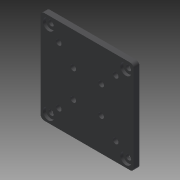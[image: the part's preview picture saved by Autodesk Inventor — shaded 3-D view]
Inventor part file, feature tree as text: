
AUTODESK INVENTOR PART (.ipt)
format: ipt  version: 2015 (Build 190159000, 159)  size: 139,264 bytes
history: native  units: mm
features: extrude x2, sketch x1, fillet x1
ambient origin geometry x8: Origin, YZ Plane, XZ Plane, XY Plane, X Axis, Y Axis, Z Axis, Center Point
bodies: Solid1 (feature_tree)
feature tree (4):
  sketch  "Sketch1"  dims[d2=3.0mm d3=3.0mm d4=3.0mm d5=3.0mm d6=50.0mm d7=50.0mm d12=3.0mm d13=3.0mm d14=3.0mm d15=3.0mm d16=6.0mm d17=6.0mm d18=3.0mm d19=0.0mm d20=2.0mm d21=6.0mm d22=6.0mm d23=6.0mm d24=6.0mm d25=1.5mm d26=0.0mm]
  extrude  "Extrusion1"  Depth=3.0mm
  fillet  "Fillet1"  Radius=3.0mm
  extrude  "Extrusion2"  Depth=3.0mm
